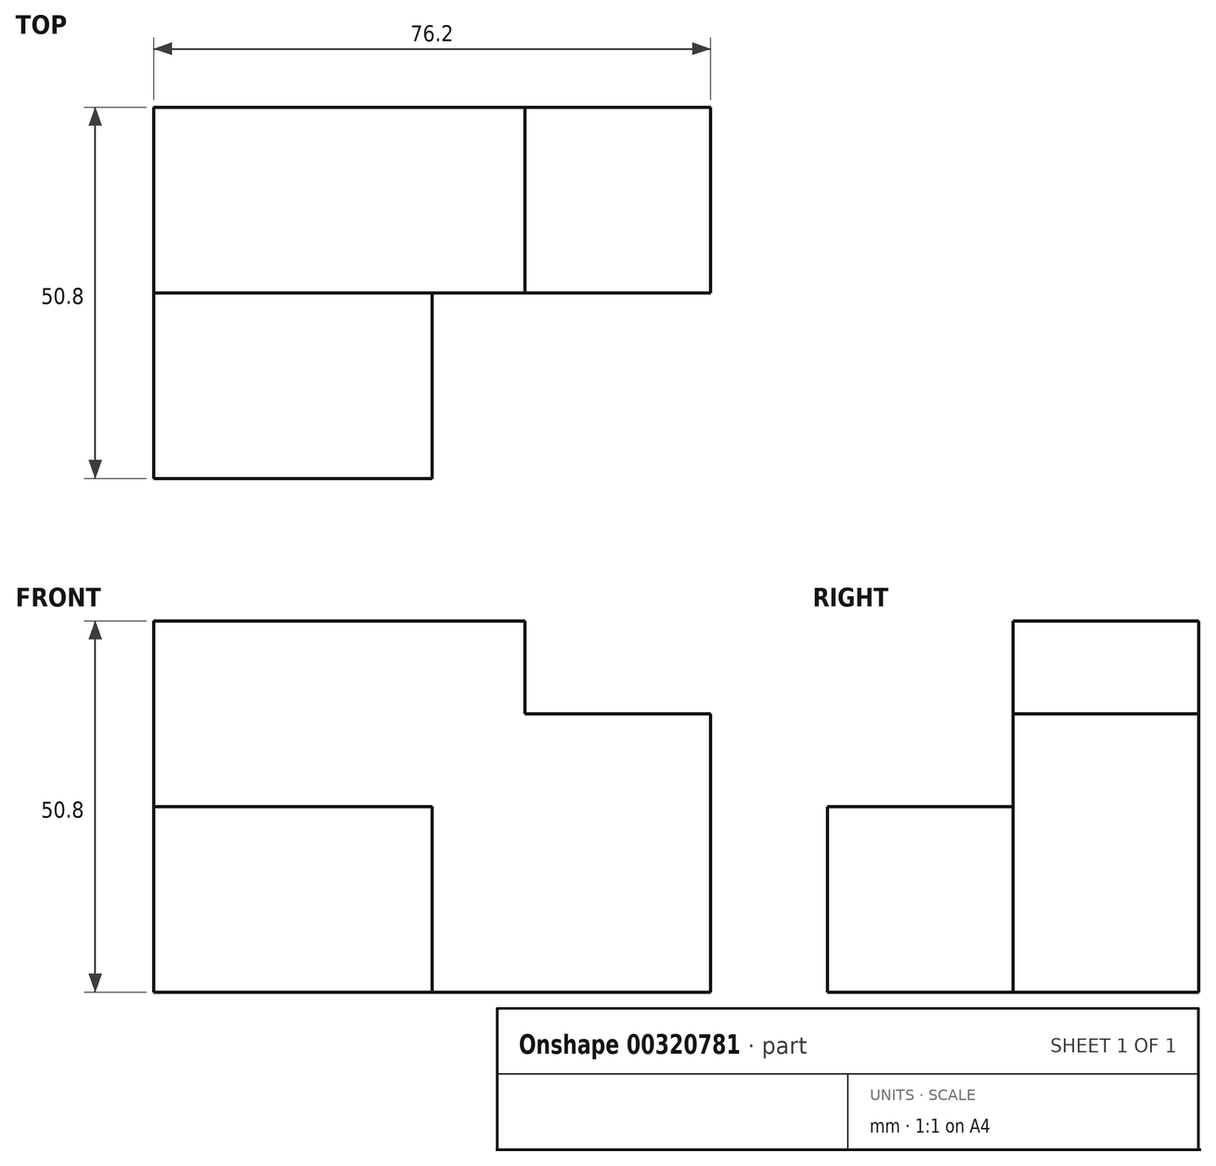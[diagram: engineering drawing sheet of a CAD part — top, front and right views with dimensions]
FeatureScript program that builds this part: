
annotation { "Feature Type Name" : "Feature", "Feature Type Description" : "" }
export const myFeature = defineFeature(function(context is Context, id is Id, definition is map)
    precondition{}
    {
        {
            var Q0;
            Q0=qCreatedBy(makeId("Right.planeOp"),FACE);
            var sketch = newSketch(context, id + "F0", { "sketchPlane" : qUnion([Q0])});
            skLineSegment(sketch, "E0", {"start": v(-8.15, 3.01) * mm, "end": v(-33.55, 3.01) * mm});
            skLineSegment(sketch, "E1", {"start": v(-33.55, 3.01) * mm, "end": v(-33.55, -22.39) * mm});
            skLineSegment(sketch, "E2", {"start": v(-33.55, -22.39) * mm, "end": v(-58.95, -22.39) * mm});
            skLineSegment(sketch, "E3", {"start": v(-58.95, -22.39) * mm, "end": v(-58.95, -47.79) * mm});
            skLineSegment(sketch, "E4", {"start": v(-58.95, -47.79) * mm, "end": v(-8.15, -47.79) * mm});
            skLineSegment(sketch, "E5", {"start": v(-8.15, -47.79) * mm, "end": v(-8.15, 3.01) * mm});
            skSolve(sketch);
        }
        {
            var Q0;
            Q0=makeQuery(id+"F0.imprint","IMPRINT",FACE,{"disambiguationData":[TD([[makeQuery(id+"F0.imprint","IMPRINT",EDGE,{"derivedFrom":sQuery(id+"F0.wireOp",EDGE,"E0")}),1.0]])]});
            extrude(context, id + "F1", {"entities" : qUnion([Q0]), "depth" : 76.2 * mm});
        }
        {
            var Q0;
            Q0=makeQuery(id+"F1.opExtrude","SWEPT_FACE",FACE,{"disambiguationData":[OSD([sQuery(id+"F0.wireOp",EDGE,"E1")])]});
            var sketch = newSketch(context, id + "F2", { "sketchPlane" : qUnion([Q0])});
            skLineSegment(sketch, "E6", {"start": v(50.8, 3.01) * mm, "end": v(50.8, -9.69) * mm});
            skLineSegment(sketch, "E7", {"start": v(50.8, -9.69) * mm, "end": v(76.2, -9.69) * mm});
            skLineSegment(sketch, "E8", {"start": v(76.2, -9.69) * mm, "end": v(76.2, 3.01) * mm});
            skLineSegment(sketch, "E9", {"start": v(76.2, 3.01) * mm, "end": v(50.8, 3.01) * mm});
            skSolve(sketch);
        }
        {
            var Q0;
            Q0=makeQuery(id+"F2.imprint","IMPRINT",FACE,{"disambiguationData":[TD([[makeQuery(id+"F2.imprint","IMPRINT",EDGE,{"derivedFrom":sQuery(id+"F2.wireOp",EDGE,"E6")}),1.0]])]});
            extrude(context, id + "F3", {"entities" : qUnion([Q0]), "operationType" : NewBodyOperationType.REMOVE, "oppositeDirection" : true, "depth" : 47.24 * mm});
        }
        {
            var Q0;
            Q0=makeQuery(id+"F1.opExtrude","SWEPT_FACE",FACE,{"disambiguationData":[OSD([sQuery(id+"F0.wireOp",EDGE,"E3")])]});
            var sketch = newSketch(context, id + "F4", { "sketchPlane" : qUnion([Q0])});
            skLineSegment(sketch, "E10", {"start": v(38.1, -22.39) * mm, "end": v(38.1, -47.79) * mm});
            skLineSegment(sketch, "E11", {"start": v(38.1, -47.79) * mm, "end": v(76.2, -47.79) * mm});
            skLineSegment(sketch, "E12", {"start": v(76.2, -47.79) * mm, "end": v(76.2, -22.39) * mm});
            skLineSegment(sketch, "E13", {"start": v(76.2, -22.39) * mm, "end": v(38.1, -22.39) * mm});
            skSolve(sketch);
        }
        {
            var Q0;
            Q0=makeQuery(id+"F4.imprint","IMPRINT",FACE,{"disambiguationData":[TD([[makeQuery(id+"F4.imprint","IMPRINT",EDGE,{"derivedFrom":sQuery(id+"F4.wireOp",EDGE,"E10")}),1.0]])]});
            extrude(context, id + "F5", {"entities" : qUnion([Q0]), "operationType" : NewBodyOperationType.REMOVE, "oppositeDirection" : true, "depth" : 25.4 * mm});
        }
    });
